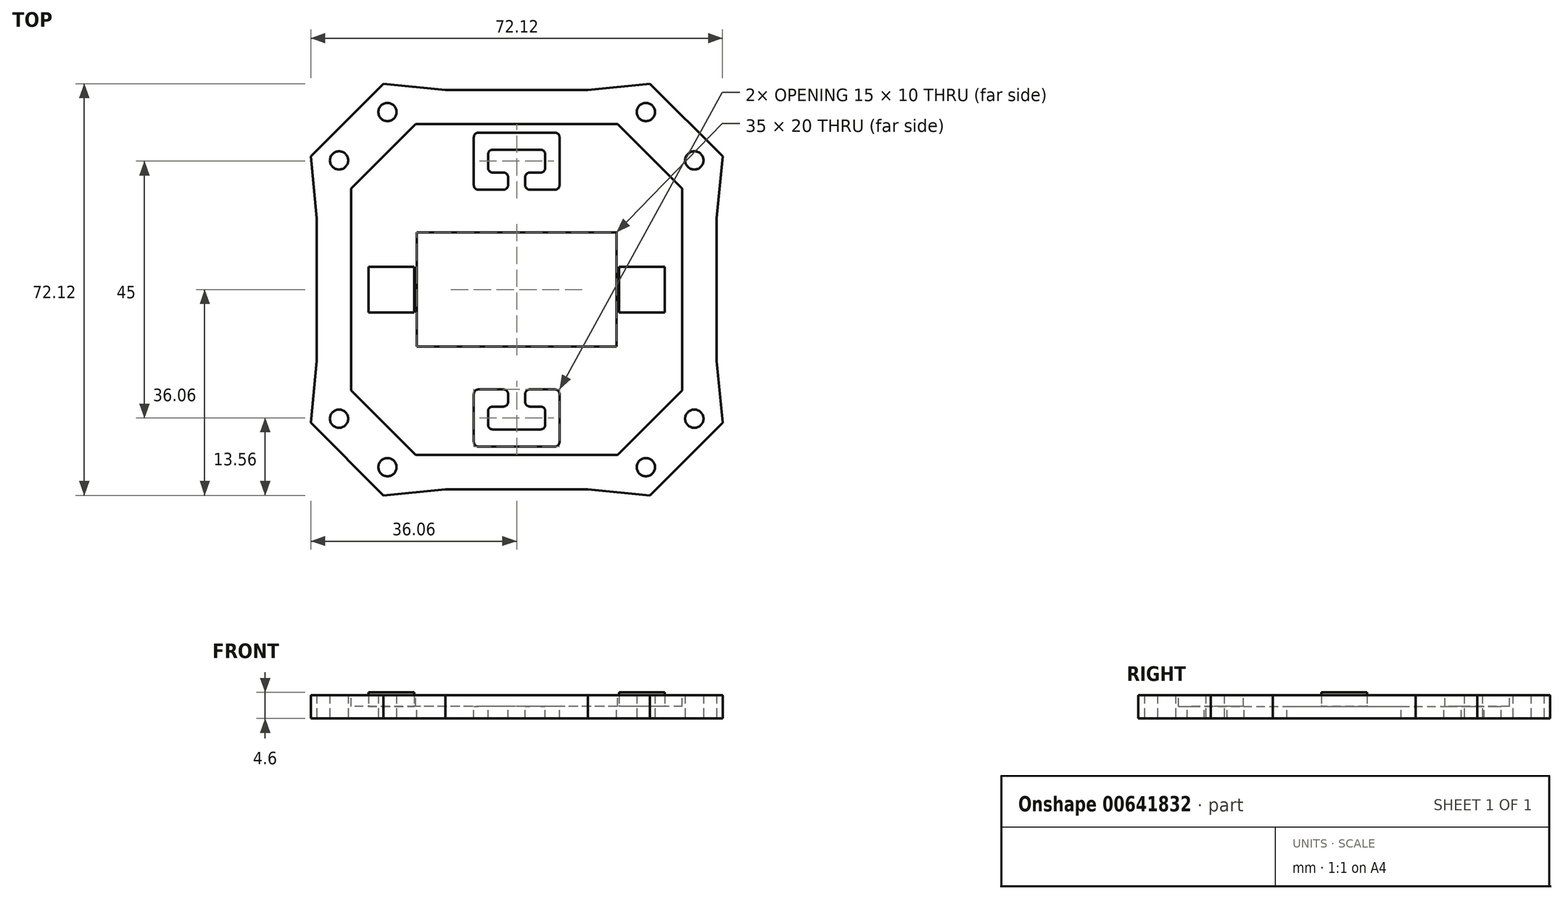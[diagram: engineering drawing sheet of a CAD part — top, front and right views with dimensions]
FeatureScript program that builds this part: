
annotation { "Feature Type Name" : "Feature", "Feature Type Description" : "" }
export const myFeature = defineFeature(function(context is Context, id is Id, definition is map)
    precondition{}
    {
        {
            var Q0;
            Q0=qCreatedBy(makeId("Top.planeOp"),FACE);
            var sketch = newSketch(context, id + "F0", { "sketchPlane" : qUnion([Q0])});
            skPoint(sketch, "E0.middle", {"position": v(0, 0) * mm});
            skLineSegment(sketch, "E1", {"start": v(0, 0) * mm, "end": v(84.85, 84.85) * mm});
            skLineSegment(sketch, "E2", {"start": v(0, 35) * mm, "end": v(0, -35) * mm});
            skLineSegment(sketch, "E3", {"start": v(-12.5, 35) * mm, "end": v(12.5, 35) * mm});
            skLineSegment(sketch, "E4.1.0", {"start": v(-35, -12.5) * mm, "end": v(-35, 12.5) * mm});
            skLineSegment(sketch, "E4.2.0", {"start": v(12.5, -35) * mm, "end": v(-12.5, -35) * mm});
            skLineSegment(sketch, "E4.3.0", {"start": v(35, 12.5) * mm, "end": v(35, -12.5) * mm});
            skLineSegment(sketch, "E5", {"start": v(20.5, 33.23) * mm, "end": v(33.23, 20.5) * mm});
            skLineSegment(sketch, "E6", {"start": v(23.33, 36.06) * mm, "end": v(36.06, 23.33) * mm});
            skLineSegment(sketch, "E7", {"start": v(12.5, 35) * mm, "end": v(23.33, 36.06) * mm});
            skLineSegment(sketch, "E8", {"start": v(35, 12.5) * mm, "end": v(36.06, 23.33) * mm});
            skCircle(sketch, "E9", {"center": v(22.63, 31.11) * mm, "radius": 1.6 * mm});
            skCircle(sketch, "E10", {"center": v(31.11, 22.63) * mm, "radius": 1.6 * mm});
            skLineSegment(sketch, "E11.1.0", {"start": v(-35, 12.5) * mm, "end": v(-36.06, 23.33) * mm});
            skLineSegment(sketch, "E11.1.1", {"start": v(-36.06, 23.33) * mm, "end": v(-23.33, 36.06) * mm});
            skCircle(sketch, "E11.1.2", {"center": v(-22.63, 31.11) * mm, "radius": 1.6 * mm});
            skCircle(sketch, "E11.1.3", {"center": v(-31.11, 22.63) * mm, "radius": 1.6 * mm});
            skLineSegment(sketch, "E11.1.4", {"start": v(-12.5, 35) * mm, "end": v(-23.33, 36.06) * mm});
            skLineSegment(sketch, "E11.2.0", {"start": v(-12.5, -35) * mm, "end": v(-23.33, -36.06) * mm});
            skLineSegment(sketch, "E11.2.1", {"start": v(-23.33, -36.06) * mm, "end": v(-36.06, -23.33) * mm});
            skCircle(sketch, "E11.2.2", {"center": v(-31.11, -22.63) * mm, "radius": 1.6 * mm});
            skCircle(sketch, "E11.2.3", {"center": v(-22.63, -31.11) * mm, "radius": 1.6 * mm});
            skLineSegment(sketch, "E11.2.4", {"start": v(-35, -12.5) * mm, "end": v(-36.06, -23.33) * mm});
            skLineSegment(sketch, "E11.3.0", {"start": v(35, -12.5) * mm, "end": v(36.06, -23.33) * mm});
            skLineSegment(sketch, "E11.3.1", {"start": v(36.06, -23.33) * mm, "end": v(23.33, -36.06) * mm});
            skCircle(sketch, "E11.3.2", {"center": v(22.63, -31.11) * mm, "radius": 1.6 * mm});
            skCircle(sketch, "E11.3.3", {"center": v(31.11, -22.63) * mm, "radius": 1.6 * mm});
            skLineSegment(sketch, "E11.3.4", {"start": v(12.5, -35) * mm, "end": v(23.33, -36.06) * mm});
            skSolve(sketch);
        }
        {
            var Q0;
            Q0=qSketchRegion(id+"F0",true);
            extrude(context, id + "F1", {"entities" : qUnion([Q0]), "depth" : 4.1 * mm, "offsetDistance" : 25 * mm});
        }
        {
            var Q0;
            Q0=makeQuery(id+"F1.opExtrude","CAP_FACE",FACE,{"disambiguationData":[OSD([sQuery(id+"F0.wireOp",EDGE,"E3"),sQuery(id+"F0.wireOp",EDGE,"E4.1.0"),sQuery(id+"F0.wireOp",EDGE,"E4.2.0"),sQuery(id+"F0.wireOp",EDGE,"E4.3.0"),sQuery(id+"F0.wireOp",EDGE,"E6"),sQuery(id+"F0.wireOp",EDGE,"E7"),sQuery(id+"F0.wireOp",EDGE,"E8"),sQuery(id+"F0.wireOp",EDGE,"E9"),sQuery(id+"F0.wireOp",EDGE,"E10"),sQuery(id+"F0.wireOp",EDGE,"E11.1.0"),sQuery(id+"F0.wireOp",EDGE,"E11.1.1"),sQuery(id+"F0.wireOp",EDGE,"E11.1.2"),sQuery(id+"F0.wireOp",EDGE,"E11.1.3"),sQuery(id+"F0.wireOp",EDGE,"E11.1.4"),sQuery(id+"F0.wireOp",EDGE,"E11.2.0"),sQuery(id+"F0.wireOp",EDGE,"E11.2.1"),sQuery(id+"F0.wireOp",EDGE,"E11.2.2"),sQuery(id+"F0.wireOp",EDGE,"E11.2.3"),sQuery(id+"F0.wireOp",EDGE,"E11.2.4"),sQuery(id+"F0.wireOp",EDGE,"E11.3.0"),sQuery(id+"F0.wireOp",EDGE,"E11.3.1"),sQuery(id+"F0.wireOp",EDGE,"E11.3.2"),sQuery(id+"F0.wireOp",EDGE,"E11.3.3"),sQuery(id+"F0.wireOp",EDGE,"E11.3.4")])],"isStart":false});
            var sketch = newSketch(context, id + "F2", { "sketchPlane" : qUnion([Q0])});
            skLineSegment(sketch, "E12", {"start": v(-35, 0) * mm, "end": v(0, 0) * mm});
            skLineSegment(sketch, "E13", {"start": v(0, 0) * mm, "end": v(0, 35) * mm});
            skLineSegment(sketch, "E14", {"start": v(-17.67, 29) * mm, "end": v(17.67, 29) * mm});
            skLineSegment(sketch, "E15", {"start": v(17.67, 29) * mm, "end": v(29, 17.67) * mm});
            skLineSegment(sketch, "E16", {"start": v(29, 17.67) * mm, "end": v(29, -17.67) * mm});
            skLineSegment(sketch, "E17", {"start": v(29, -17.67) * mm, "end": v(17.67, -29) * mm});
            skLineSegment(sketch, "E18", {"start": v(17.67, -29) * mm, "end": v(-17.67, -29) * mm});
            skLineSegment(sketch, "E19", {"start": v(-17.67, -29) * mm, "end": v(-29, -17.67) * mm});
            skLineSegment(sketch, "E20", {"start": v(-29, -17.67) * mm, "end": v(-29, 17.67) * mm});
            skLineSegment(sketch, "E21", {"start": v(-29, 17.67) * mm, "end": v(-17.67, 29) * mm});
            skSolve(sketch);
        }
        {
            var Q0;
            Q0=qSketchRegion(id+"F2",true);
            extrude(context, id + "F3", {"entities" : qUnion([Q0]), "operationType" : NewBodyOperationType.REMOVE, "oppositeDirection" : true, "depth" : 2 * mm, "offsetDistance" : 25 * mm});
        }
        {
            var Q0;
            Q0=makeQuery(id+"F3.boolean.opBoolean","COPY",FACE,{"derivedFrom":makeQuery(id+"F3.opExtrude","CAP_FACE",FACE,{"disambiguationData":[OSD([sQuery(id+"F2.wireOp",EDGE,"E14"),sQuery(id+"F2.wireOp",EDGE,"E15"),sQuery(id+"F2.wireOp",EDGE,"E16"),sQuery(id+"F2.wireOp",EDGE,"E17"),sQuery(id+"F2.wireOp",EDGE,"E18"),sQuery(id+"F2.wireOp",EDGE,"E19"),sQuery(id+"F2.wireOp",EDGE,"E20"),sQuery(id+"F2.wireOp",EDGE,"E21")])],"isStart":false})});
            var sketch = newSketch(context, id + "F4", { "sketchPlane" : qUnion([Q0])});
            skLineSegment(sketch, "E22", {"start": v(0, 28) * mm, "end": v(0, 0) * mm});
            skLineSegment(sketch, "E23", {"start": v(0, 0) * mm, "end": v(-28, 0) * mm});
            skLineSegment(sketch, "E24.bottom", {"start": v(6.7, 17.5) * mm, "end": v(2.3, 17.5) * mm});
            skLineSegment(sketch, "E24.top", {"start": v(6.7, 27.5) * mm, "end": v(-6.7, 27.5) * mm});
            skLineSegment(sketch, "E24.left", {"start": v(7.5, 18.3) * mm, "end": v(7.5, 26.7) * mm});
            skLineSegment(sketch, "E24.right", {"start": v(-7.5, 18.3) * mm, "end": v(-7.5, 26.7) * mm});
            skPoint(sketch, "E24.middle", {"position": v(0, 22.5) * mm});
            skLineSegment(sketch, "E25.bottom", {"start": v(4.2, 20.5) * mm, "end": v(2.3, 20.5) * mm});
            skLineSegment(sketch, "E25.top", {"start": v(4.2, 24.5) * mm, "end": v(-4.2, 24.5) * mm});
            skLineSegment(sketch, "E25.left", {"start": v(5, 21.3) * mm, "end": v(5, 23.7) * mm});
            skLineSegment(sketch, "E25.right", {"start": v(-5, 21.3) * mm, "end": v(-5, 23.7) * mm});
            skLineSegment(sketch, "E26", {"start": v(-1.5, 19.7) * mm, "end": v(-1.5, 18.3) * mm});
            skLineSegment(sketch, "E27.MirrorCS", {"start": v(1.5, 19.7) * mm, "end": v(1.5, 18.3) * mm});
            skLineSegment(sketch, "E28.trimOffspring", {"start": v(-2.3, 20.5) * mm, "end": v(-4.2, 20.5) * mm});
            skLineSegment(sketch, "E29.trimOffspring", {"start": v(-2.3, 17.5) * mm, "end": v(-6.7, 17.5) * mm});
            skPoint(sketch, "E30.visualSharp", {"position": v(-7.5, 27.5) * mm});
            skArc(sketch, "E30.filletArc", {"start": v(-6.7, 27.5) * mm, "mid": v(-7.27, 27.27) * mm, "end": v(-7.5, 26.7) * mm});
            skPoint(sketch, "E31.visualSharp", {"position": v(7.5, 27.5) * mm});
            skArc(sketch, "E31.filletArc", {"start": v(7.5, 26.7) * mm, "mid": v(7.27, 27.27) * mm, "end": v(6.7, 27.5) * mm});
            skPoint(sketch, "E32.visualSharp", {"position": v(5, 24.5) * mm});
            skArc(sketch, "E32.filletArc", {"start": v(5, 23.7) * mm, "mid": v(4.77, 24.27) * mm, "end": v(4.2, 24.5) * mm});
            skPoint(sketch, "E33.visualSharp", {"position": v(5, 20.5) * mm});
            skArc(sketch, "E33.filletArc", {"start": v(4.2, 20.5) * mm, "mid": v(4.77, 20.73) * mm, "end": v(5, 21.3) * mm});
            skPoint(sketch, "E34.visualSharp", {"position": v(-5, 24.5) * mm});
            skArc(sketch, "E34.filletArc", {"start": v(-4.2, 24.5) * mm, "mid": v(-4.77, 24.27) * mm, "end": v(-5, 23.7) * mm});
            skPoint(sketch, "E35.visualSharp", {"position": v(-5, 20.5) * mm});
            skArc(sketch, "E35.filletArc", {"start": v(-5, 21.3) * mm, "mid": v(-4.77, 20.73) * mm, "end": v(-4.2, 20.5) * mm});
            skPoint(sketch, "E36.visualSharp", {"position": v(-1.5, 20.5) * mm});
            skArc(sketch, "E36.filletArc", {"start": v(-1.5, 19.7) * mm, "mid": v(-1.73, 20.27) * mm, "end": v(-2.3, 20.5) * mm});
            skPoint(sketch, "E37.visualSharp", {"position": v(-7.5, 17.5) * mm});
            skArc(sketch, "E37.filletArc", {"start": v(-7.5, 18.3) * mm, "mid": v(-7.27, 17.73) * mm, "end": v(-6.7, 17.5) * mm});
            skPoint(sketch, "E38.visualSharp", {"position": v(-1.5, 17.5) * mm});
            skArc(sketch, "E38.filletArc", {"start": v(-2.3, 17.5) * mm, "mid": v(-1.73, 17.73) * mm, "end": v(-1.5, 18.3) * mm});
            skPoint(sketch, "E39.visualSharp", {"position": v(1.5, 17.5) * mm});
            skArc(sketch, "E39.filletArc", {"start": v(1.5, 18.3) * mm, "mid": v(1.73, 17.73) * mm, "end": v(2.3, 17.5) * mm});
            skPoint(sketch, "E40.visualSharp", {"position": v(1.5, 20.5) * mm});
            skArc(sketch, "E40.filletArc", {"start": v(2.3, 20.5) * mm, "mid": v(1.73, 20.27) * mm, "end": v(1.5, 19.7) * mm});
            skPoint(sketch, "E41.visualSharp", {"position": v(7.5, 17.5) * mm});
            skArc(sketch, "E41.filletArc", {"start": v(6.7, 17.5) * mm, "mid": v(7.27, 17.73) * mm, "end": v(7.5, 18.3) * mm});
            skArc(sketch, "E42.MirrorCS", {"start": v(6.7, 27.5) * mm, "mid": v(7.27, 27.27) * mm, "end": v(7.5, 26.7) * mm});
            skArc(sketch, "E43.MirrorCS", {"start": v(7.5, 18.3) * mm, "mid": v(7.27, 17.73) * mm, "end": v(6.7, 17.5) * mm});
            skArc(sketch, "E44.MirrorCS", {"start": v(4.2, 24.5) * mm, "mid": v(4.77, 24.27) * mm, "end": v(5, 23.7) * mm});
            skArc(sketch, "E45.MirrorCS", {"start": v(-5, 23.7) * mm, "mid": v(-4.77, 24.27) * mm, "end": v(-4.2, 24.5) * mm});
            skArc(sketch, "E46.MirrorCS", {"start": v(-1.5, 18.3) * mm, "mid": v(-1.73, 17.73) * mm, "end": v(-2.3, 17.5) * mm});
            skArc(sketch, "E47.MirrorCS", {"start": v(2.3, 17.5) * mm, "mid": v(1.73, 17.73) * mm, "end": v(1.5, 18.3) * mm});
            skArc(sketch, "E48.MirrorCS", {"start": v(-6.7, 17.5) * mm, "mid": v(-7.27, 17.73) * mm, "end": v(-7.5, 18.3) * mm});
            skArc(sketch, "E49.MirrorCS", {"start": v(-4.2, 20.5) * mm, "mid": v(-4.77, 20.73) * mm, "end": v(-5, 21.3) * mm});
            skArc(sketch, "E50.MirrorCS", {"start": v(5, 21.3) * mm, "mid": v(4.77, 20.73) * mm, "end": v(4.2, 20.5) * mm});
            skArc(sketch, "E51.MirrorCS", {"start": v(1.5, 19.7) * mm, "mid": v(1.73, 20.27) * mm, "end": v(2.3, 20.5) * mm});
            skArc(sketch, "E52.MirrorCS", {"start": v(-2.3, 20.5) * mm, "mid": v(-1.73, 20.27) * mm, "end": v(-1.5, 19.7) * mm});
            skArc(sketch, "E53.MirrorCS", {"start": v(-7.5, 26.7) * mm, "mid": v(-7.27, 27.27) * mm, "end": v(-6.7, 27.5) * mm});
            skLineSegment(sketch, "E54.MirrorCS", {"start": v(-4.2, 20.5) * mm, "end": v(-2.3, 20.5) * mm});
            skLineSegment(sketch, "E55.MirrorCS", {"start": v(-6.7, 17.5) * mm, "end": v(-2.3, 17.5) * mm});
            skLineSegment(sketch, "E56.MirrorCS", {"start": v(-4.2, 24.5) * mm, "end": v(4.2, 24.5) * mm});
            skLineSegment(sketch, "E57.MirrorCS", {"start": v(2.3, 20.5) * mm, "end": v(4.2, 20.5) * mm});
            skLineSegment(sketch, "E58.MirrorCS", {"start": v(2.3, 17.5) * mm, "end": v(6.7, 17.5) * mm});
            skLineSegment(sketch, "E59.MirrorCS", {"start": v(-6.7, 27.5) * mm, "end": v(6.7, 27.5) * mm});
            skArc(sketch, "E60.MirrorCS", {"start": v(-2.3, -20.5) * mm, "mid": v(-1.73, -20.27) * mm, "end": v(-1.5, -19.7) * mm});
            skLineSegment(sketch, "E61.MirrorCS", {"start": v(1.5, -19.7) * mm, "end": v(1.5, -18.3) * mm});
            skArc(sketch, "E62.MirrorCS", {"start": v(-1.5, -19.7) * mm, "mid": v(-1.73, -20.27) * mm, "end": v(-2.3, -20.5) * mm});
            skArc(sketch, "E63.MirrorCS", {"start": v(-7.5, -26.7) * mm, "mid": v(-7.27, -27.27) * mm, "end": v(-6.7, -27.5) * mm});
            skArc(sketch, "E64.MirrorCS", {"start": v(-4.2, -20.5) * mm, "mid": v(-4.77, -20.73) * mm, "end": v(-5, -21.3) * mm});
            skArc(sketch, "E65.MirrorCS", {"start": v(2.3, -20.5) * mm, "mid": v(1.73, -20.27) * mm, "end": v(1.5, -19.7) * mm});
            skArc(sketch, "E66.MirrorCS", {"start": v(6.7, -27.5) * mm, "mid": v(7.27, -27.27) * mm, "end": v(7.5, -26.7) * mm});
            skArc(sketch, "E67.MirrorCS", {"start": v(-4.2, -24.5) * mm, "mid": v(-4.77, -24.27) * mm, "end": v(-5, -23.7) * mm});
            skArc(sketch, "E68.MirrorCS", {"start": v(1.5, -19.7) * mm, "mid": v(1.73, -20.27) * mm, "end": v(2.3, -20.5) * mm});
            skArc(sketch, "E69.MirrorCS", {"start": v(-1.5, -18.3) * mm, "mid": v(-1.73, -17.73) * mm, "end": v(-2.3, -17.5) * mm});
            skArc(sketch, "E70.MirrorCS", {"start": v(-5, -21.3) * mm, "mid": v(-4.77, -20.73) * mm, "end": v(-4.2, -20.5) * mm});
            skArc(sketch, "E71.MirrorCS", {"start": v(-6.7, -27.5) * mm, "mid": v(-7.27, -27.27) * mm, "end": v(-7.5, -26.7) * mm});
            skLineSegment(sketch, "E72.MirrorCS", {"start": v(-1.5, -19.7) * mm, "end": v(-1.5, -18.3) * mm});
            skLineSegment(sketch, "E73.MirrorCS", {"start": v(2.3, -20.5) * mm, "end": v(4.2, -20.5) * mm});
            skArc(sketch, "E74.MirrorCS", {"start": v(6.7, -17.5) * mm, "mid": v(7.27, -17.73) * mm, "end": v(7.5, -18.3) * mm});
            skLineSegment(sketch, "E75.MirrorCS", {"start": v(-4.2, -20.5) * mm, "end": v(-2.3, -20.5) * mm});
            skArc(sketch, "E76.MirrorCS", {"start": v(5, -23.7) * mm, "mid": v(4.77, -24.27) * mm, "end": v(4.2, -24.5) * mm});
            skArc(sketch, "E77.MirrorCS", {"start": v(4.2, -20.5) * mm, "mid": v(4.77, -20.73) * mm, "end": v(5, -21.3) * mm});
            skArc(sketch, "E78.MirrorCS", {"start": v(-6.7, -17.5) * mm, "mid": v(-7.27, -17.73) * mm, "end": v(-7.5, -18.3) * mm});
            skArc(sketch, "E79.MirrorCS", {"start": v(1.5, -18.3) * mm, "mid": v(1.73, -17.73) * mm, "end": v(2.3, -17.5) * mm});
            skArc(sketch, "E80.MirrorCS", {"start": v(7.5, -26.7) * mm, "mid": v(7.27, -27.27) * mm, "end": v(6.7, -27.5) * mm});
            skArc(sketch, "E81.MirrorCS", {"start": v(-7.5, -18.3) * mm, "mid": v(-7.27, -17.73) * mm, "end": v(-6.7, -17.5) * mm});
            skArc(sketch, "E82.MirrorCS", {"start": v(4.2, -24.5) * mm, "mid": v(4.77, -24.27) * mm, "end": v(5, -23.7) * mm});
            skArc(sketch, "E83.MirrorCS", {"start": v(-5, -23.7) * mm, "mid": v(-4.77, -24.27) * mm, "end": v(-4.2, -24.5) * mm});
            skArc(sketch, "E84.MirrorCS", {"start": v(2.3, -17.5) * mm, "mid": v(1.73, -17.73) * mm, "end": v(1.5, -18.3) * mm});
            skLineSegment(sketch, "E85.MirrorCS", {"start": v(4.2, -20.5) * mm, "end": v(2.3, -20.5) * mm});
            skArc(sketch, "E86.MirrorCS", {"start": v(-2.3, -17.5) * mm, "mid": v(-1.73, -17.73) * mm, "end": v(-1.5, -18.3) * mm});
            skArc(sketch, "E87.MirrorCS", {"start": v(7.5, -18.3) * mm, "mid": v(7.27, -17.73) * mm, "end": v(6.7, -17.5) * mm});
            skArc(sketch, "E88.MirrorCS", {"start": v(5, -21.3) * mm, "mid": v(4.77, -20.73) * mm, "end": v(4.2, -20.5) * mm});
            skLineSegment(sketch, "E89.MirrorCS", {"start": v(-2.3, -20.5) * mm, "end": v(-4.2, -20.5) * mm});
            skPoint(sketch, "E90.MirrorP", {"position": v(0, -22.5) * mm});
            skPoint(sketch, "E91.MirrorP", {"position": v(-7.5, -17.5) * mm});
            skLineSegment(sketch, "E92.MirrorCS", {"start": v(7.5, -18.3) * mm, "end": v(7.5, -26.7) * mm});
            skLineSegment(sketch, "E93.MirrorCS", {"start": v(2.3, -17.5) * mm, "end": v(6.7, -17.5) * mm});
            skLineSegment(sketch, "E94.MirrorCS", {"start": v(-7.5, -18.3) * mm, "end": v(-7.5, -26.7) * mm});
            skPoint(sketch, "E95.MirrorP", {"position": v(-7.5, -27.5) * mm});
            skLineSegment(sketch, "E96.MirrorCS", {"start": v(-5, -21.3) * mm, "end": v(-5, -23.7) * mm});
            skPoint(sketch, "E97.MirrorP", {"position": v(1.5, -20.5) * mm});
            skPoint(sketch, "E98.MirrorP", {"position": v(-1.5, -17.5) * mm});
            skPoint(sketch, "E99.MirrorP", {"position": v(5, -24.5) * mm});
            skLineSegment(sketch, "E100.MirrorCS", {"start": v(-6.7, -27.5) * mm, "end": v(6.7, -27.5) * mm});
            skPoint(sketch, "E101.MirrorP", {"position": v(7.5, -27.5) * mm});
            skLineSegment(sketch, "E102.MirrorCS", {"start": v(-4.2, -24.5) * mm, "end": v(4.2, -24.5) * mm});
            skPoint(sketch, "E103.MirrorP", {"position": v(-5, -24.5) * mm});
            skLineSegment(sketch, "E104.MirrorCS", {"start": v(5, -21.3) * mm, "end": v(5, -23.7) * mm});
            skPoint(sketch, "E105.MirrorP", {"position": v(7.5, -17.5) * mm});
            skPoint(sketch, "E106.MirrorP", {"position": v(5, -20.5) * mm});
            skPoint(sketch, "E107.MirrorP", {"position": v(1.5, -17.5) * mm});
            skPoint(sketch, "E108.MirrorP", {"position": v(-1.5, -20.5) * mm});
            skLineSegment(sketch, "E109.MirrorCS", {"start": v(-6.7, -17.5) * mm, "end": v(-2.3, -17.5) * mm});
            skPoint(sketch, "E110.MirrorP", {"position": v(-5, -20.5) * mm});
            skLineSegment(sketch, "E111.MirrorCS", {"start": v(6.7, -27.5) * mm, "end": v(-6.7, -27.5) * mm});
            skLineSegment(sketch, "E112.MirrorCS", {"start": v(6.7, -17.5) * mm, "end": v(2.3, -17.5) * mm});
            skLineSegment(sketch, "E113.MirrorCS", {"start": v(4.2, -24.5) * mm, "end": v(-4.2, -24.5) * mm});
            skLineSegment(sketch, "E114.MirrorCS", {"start": v(-2.3, -17.5) * mm, "end": v(-6.7, -17.5) * mm});
            skSolve(sketch);
        }
        {
            var Q0;
            Q0 = qSketchRegion(id + "F4", true);
            extrude(context, id + "F5", {"entities" : qUnion([Q0]), "operationType" : NewBodyOperationType.REMOVE, "endBound" : BoundingType.THROUGH_ALL, "oppositeDirection" : true, "depth" : 25 * mm, "offsetDistance" : 25 * mm});
        }
        {
            var Q0;
            Q0=makeQuery(id+"F3.boolean.opBoolean","COPY",FACE,{"derivedFrom":makeQuery(id+"F3.opExtrude","CAP_FACE",FACE,{"disambiguationData":[OSD([sQuery(id+"F2.wireOp",EDGE,"E14"),sQuery(id+"F2.wireOp",EDGE,"E15"),sQuery(id+"F2.wireOp",EDGE,"E16"),sQuery(id+"F2.wireOp",EDGE,"E17"),sQuery(id+"F2.wireOp",EDGE,"E18"),sQuery(id+"F2.wireOp",EDGE,"E19"),sQuery(id+"F2.wireOp",EDGE,"E20"),sQuery(id+"F2.wireOp",EDGE,"E21")])],"isStart":false})});
            var sketch = newSketch(context, id + "F6", { "sketchPlane" : qUnion([Q0])});
            skLineSegment(sketch, "E115.bottom", {"start": v(17.5, -10) * mm, "end": v(-17.5, -10) * mm});
            skLineSegment(sketch, "E115.top", {"start": v(17.5, 10) * mm, "end": v(-17.5, 10) * mm});
            skLineSegment(sketch, "E115.left", {"start": v(17.5, -10) * mm, "end": v(17.5, 10) * mm});
            skLineSegment(sketch, "E115.right", {"start": v(-17.5, -10) * mm, "end": v(-17.5, 10) * mm});
            skPoint(sketch, "E115.middle", {"position": v(0, 0) * mm});
            skSolve(sketch);
        }
        {
            var Q0;
            Q0 = qSketchRegion(id + "F6", true);
            extrude(context, id + "F7", {"entities" : qUnion([Q0]), "operationType" : NewBodyOperationType.REMOVE, "endBound" : BoundingType.THROUGH_ALL, "oppositeDirection" : true, "depth" : 25 * mm, "offsetDistance" : 25 * mm});
        }
        {
            var Q0;
            Q0=makeQuery(id+"F6.imprint","IMPRINT",FACE,{"disambiguationData":[TD([[makeQuery(id+"F6.imprint","IMPRINT",EDGE,{"derivedFrom":sQuery(id+"F6.wireOp",EDGE,"E115.bottom")}),1.0]])]});
            var sketch = newSketch(context, id + "F8", { "sketchPlane" : qUnion([Q0])});
            skLineSegment(sketch, "E116.bottom", {"start": v(-25.96, 4) * mm, "end": v(-17.96, 4) * mm});
            skLineSegment(sketch, "E116.top", {"start": v(-25.96, -4) * mm, "end": v(-17.96, -4) * mm});
            skLineSegment(sketch, "E116.left", {"start": v(-25.96, 4) * mm, "end": v(-25.96, -4) * mm});
            skLineSegment(sketch, "E116.right", {"start": v(-17.96, 4) * mm, "end": v(-17.96, -4) * mm});
            skLineSegment(sketch, "E117.MirrorCS", {"start": v(25.96, 4) * mm, "end": v(17.96, 4) * mm});
            skLineSegment(sketch, "E118.MirrorCS", {"start": v(25.96, 4) * mm, "end": v(25.96, -4) * mm});
            skLineSegment(sketch, "E119.MirrorCS", {"start": v(17.96, 4) * mm, "end": v(17.96, -4) * mm});
            skLineSegment(sketch, "E120.MirrorCS", {"start": v(25.96, -4) * mm, "end": v(17.96, -4) * mm});
            skSolve(sketch);
        }
        {
            var Q0;
            Q0 = qSketchRegion(id + "F8", true);
            extrude(context, id + "F9", {"entities" : qUnion([Q0]), "operationType" : NewBodyOperationType.ADD, "depth" : 2.5 * mm, "offsetDistance" : 25 * mm});
        }
    });
